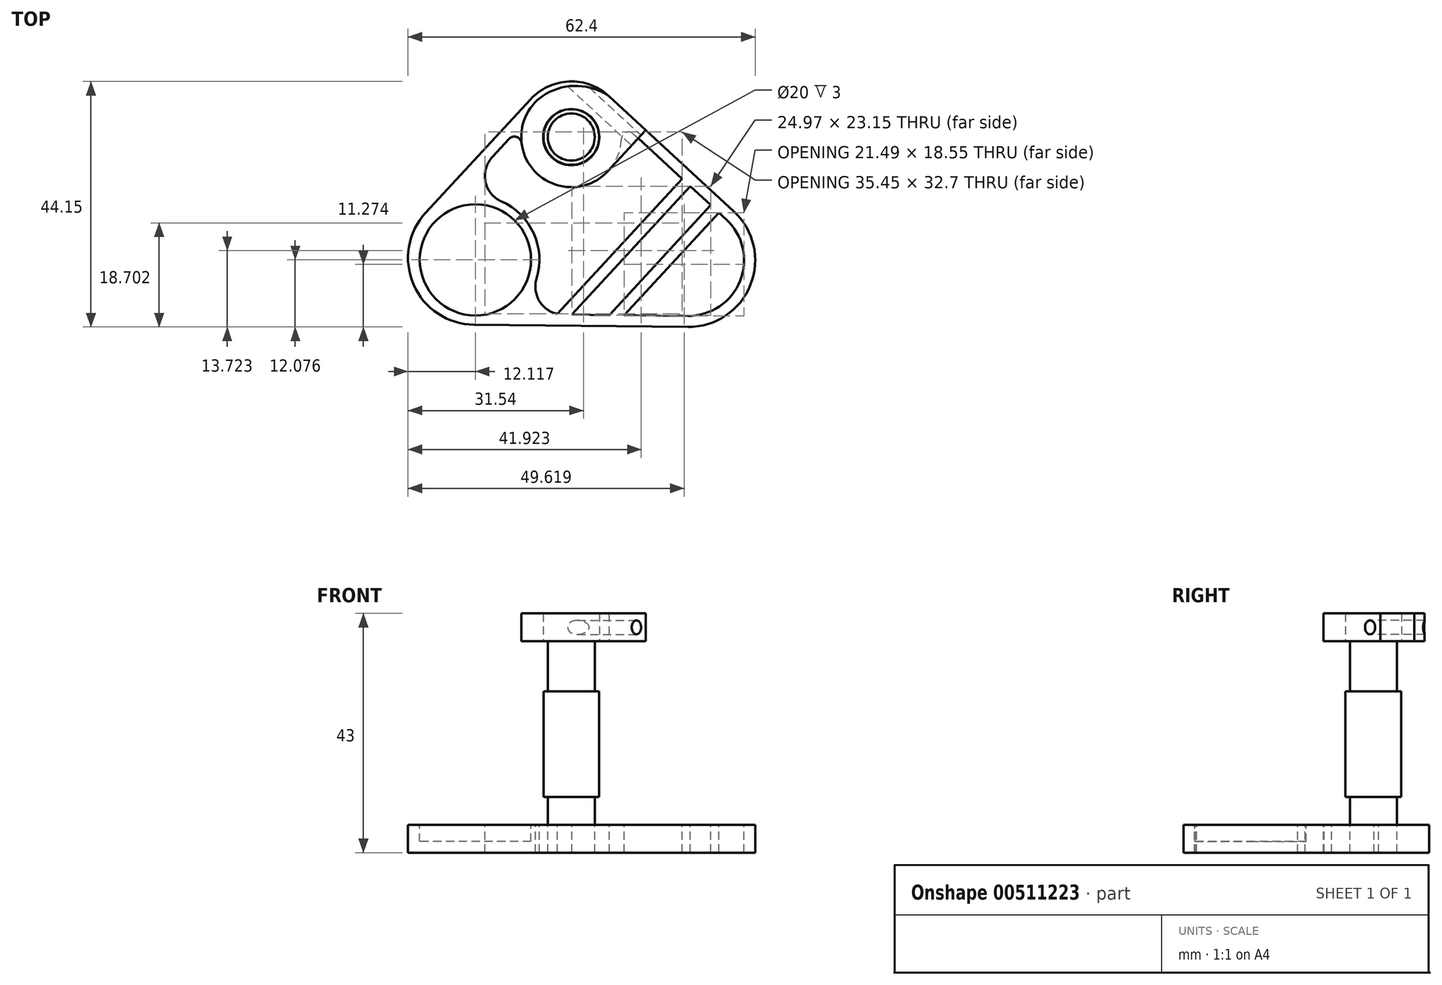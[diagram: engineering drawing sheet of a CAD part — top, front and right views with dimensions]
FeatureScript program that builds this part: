
annotation { "Feature Type Name" : "Feature", "Feature Type Description" : "" }
export const myFeature = defineFeature(function(context is Context, id is Id, definition is map)
    precondition{}
    {
        {
            var Q0;
            Q0=qCreatedBy(makeId("Top.planeOp"),FACE);
            var sketch = newSketch(context, id + "F0", { "sketchPlane" : qUnion([Q0])});
            skCircle(sketch, "E0", {"center": v(31.1, -55.05) * mm, "radius": 5 * mm});
            skCircle(sketch, "E1", {"center": v(31.1, -55.05) * mm, "radius": 4.22 * mm});
            skCircle(sketch, "E2", {"center": v(13.88, -77.12) * mm, "radius": 10 * mm});
            skPoint(sketch, "E3", {"position": v(54.93, -69.76) * mm});
            skLineSegment(sketch, "E4", {"start": v(23.76, -48.27) * mm, "end": v(4.95, -68.66) * mm});
            skLineSegment(sketch, "E5", {"start": v(37.89, -47.7) * mm, "end": v(60.3, -68.38) * mm});
            skLineSegment(sketch, "E6", {"start": v(52.03, -89.2) * mm, "end": v(13.64, -88.8) * mm});
            skArc(sketch, "E7.filletArc", {"start": v(4.95, -68.66) * mm, "mid": v(2.75, -81.55) * mm, "end": v(13.64, -88.8) * mm});
            skPoint(sketch, "E8.visualSharp", {"position": v(30.54, -40.92) * mm});
            skArc(sketch, "E8.filletArc", {"start": v(37.89, -47.7) * mm, "mid": v(30.7, -45.06) * mm, "end": v(23.76, -48.27) * mm});
            skArc(sketch, "E9.filletArc", {"start": v(52.03, -89.2) * mm, "mid": v(63.3, -81.63) * mm, "end": v(60.3, -68.38) * mm});
            skArc(sketch, "E10", {"start": v(22.17, -56.11) * mm, "mid": v(31.47, -64.05) * mm, "end": v(40.1, -55.4) * mm});
            skArc(sketch, "E11", {"start": v(24.87, -80.5) * mm, "mid": v(24.34, -72.35) * mm, "end": v(18.54, -66.61) * mm});
            skLineSegment(sketch, "E12", {"start": v(16.9, -58.65) * mm, "end": v(19.92, -55.38) * mm});
            skArc(sketch, "E13", {"start": v(52.05, -87.2) * mm, "mid": v(61.45, -80.9) * mm, "end": v(58.94, -69.85) * mm});
            skLineSegment(sketch, "E14", {"start": v(42.29, -54.48) * mm, "end": v(58.96, -69.87) * mm});
            skLineSegment(sketch, "E15", {"start": v(29.6, -86.96) * mm, "end": v(52.05, -87.2) * mm});
            skPoint(sketch, "E16.endSnap0", {"position": v(14.35, -58.46) * mm});
            skLineSegment(sketch, "E17", {"start": v(31.2, -86.98) * mm, "end": v(52.5, -63.9) * mm});
            skPoint(sketch, "E18.orphan", {"position": v(57.46, -58.46) * mm});
            skLineSegment(sketch, "E19.trimOffspring", {"start": v(28.5, -86.95) * mm, "end": v(51.02, -62.55) * mm});
            skLineSegment(sketch, "E20", {"start": v(37.94, -87.05) * mm, "end": v(56.17, -67.3) * mm});
            skLineSegment(sketch, "E21", {"start": v(40.63, -87.08) * mm, "end": v(57.64, -68.65) * mm});
            skPoint(sketch, "E22.visualSharp", {"position": v(9.76, -66.39) * mm});
            skArc(sketch, "E22.filletArc", {"start": v(16.9, -58.65) * mm, "mid": v(15.68, -63.06) * mm, "end": v(18.54, -66.61) * mm});
            skPoint(sketch, "E23.visualSharp", {"position": v(20, -86.86) * mm});
            skArc(sketch, "E23.filletArc", {"start": v(24.87, -80.5) * mm, "mid": v(25.62, -84.91) * mm, "end": v(29.6, -86.96) * mm});
            skArc(sketch, "E24.filletArc", {"start": v(22.17, -56.11) * mm, "mid": v(21.28, -55.03) * mm, "end": v(19.92, -55.38) * mm});
            skPoint(sketch, "E25.visualSharp", {"position": v(39.56, -51.97) * mm});
            skArc(sketch, "E25.filletArc", {"start": v(42.29, -54.48) * mm, "mid": v(40.9, -54.24) * mm, "end": v(40.1, -55.4) * mm});
            skSolve(sketch);
        }
        {
            var Q0;
            Q0=makeQuery(id+"F0.imprint","IMPRINT",FACE,{"disambiguationData":[TD([[makeQuery(id+"F0.imprint","IMPRINT",EDGE,{"derivedFrom":sQuery(id+"F0.wireOp",EDGE,"ScRWYDua-mYab-p1bD-zXnp-wvtpqM8LOkLs.bottom")}),-1.0]])]});
            var Q1;
            Q1=makeQuery(id+"F0.imprint","IMPRINT",FACE,{"disambiguationData":[TD([[makeQuery(id+"F0.imprint","IMPRINT",EDGE,{"derivedFrom":sQuery(id+"F0.wireOp",EDGE,"E2")}),1.0]])]});
            var Q2;
            Q2=makeQuery(id+"F0.imprint","IMPRINT",FACE,{"disambiguationData":[TD([[makeQuery(id+"F0.imprint","IMPRINT",EDGE,{"derivedFrom":sQuery(id+"F0.wireOp",EDGE,"W70nhKsN-JiaP-Kaip-Gnzn-Tj85YjjBPHD4.bottom")}),1.0]])]});
            var Q3;
            Q3=makeQuery(id+"F0.imprint","IMPRINT",FACE,{"disambiguationData":[TD([[makeQuery(id+"F0.imprint","IMPRINT",EDGE,{"derivedFrom":sQuery(id+"F0.wireOp",EDGE,"ScRWYDua-mYab-p1bD-zXnp-wvtpqM8LOkLs.top")}),1.0]])]});
            var Q4;
            Q4=makeQuery(id+"F0.imprint","IMPRINT",FACE,{"disambiguationData":[TD([[makeQuery(id+"F0.imprint","IMPRINT",EDGE,{"derivedFrom":sQuery(id+"F0.wireOp",EDGE,"E0")}),-1.0]])]});
            var Q5;
            {var subQ0=sQuery(id+"F0.wireOp",EDGE,"E17");Q5=makeQuery(id+"F0.imprint","IMPRINT",FACE,{"disambiguationData":[TD([[makeQuery(id+"F0.imprint","IMPRINT",EDGE,{"derivedFrom":subQ0}),1.0]])]});}
            var Q6;
            {var subQ0=sQuery(id+"F0.wireOp",EDGE,"E20");Q6=makeQuery(id+"F0.imprint","IMPRINT",FACE,{"disambiguationData":[TD([[makeQuery(id+"F0.imprint","IMPRINT",EDGE,{"derivedFrom":subQ0}),-1.0]])]});}
            var Q7;
            {var subQ0=sQuery(id+"F0.wireOp",EDGE,"thUjPLeQ-msCZ-fr84-VyUT-lr2uj8MLr4R7");Q7=makeQuery(id+"F0.imprint","IMPRINT",FACE,{"disambiguationData":[TD([[makeQuery(id+"F0.imprint","IMPRINT",EDGE,{"derivedFrom":subQ0}),-1.0]])]});}
            var Q8;
            Q8=makeQuery(id+"F0.imprint","IMPRINT",FACE,{"disambiguationData":[TD([[makeQuery(id+"F0.imprint","IMPRINT",EDGE,{"derivedFrom":sQuery(id+"F0.wireOp",EDGE,"E0")}),1.0]])]});
            extrude(context, id + "F1", {"entities" : qUnion([Q0, Q1, Q2, Q3, Q4, Q5, Q6, Q7, Q8]), "oppositeDirection" : true, "depth" : 5 * mm, "offsetDistance" : 25 * mm});
        }
        {
            var Q0;
            Q0=makeQuery(id+"F0.imprint","IMPRINT",FACE,{"disambiguationData":[TD([[makeQuery(id+"F0.imprint","IMPRINT",EDGE,{"derivedFrom":sQuery(id+"F0.wireOp",EDGE,"E1")}),1.0]])]});
            extrude(context, id + "F2", {"entities" : qUnion([Q0]), "depth" : 33 * mm, "offsetDistance" : 25 * mm});
        }
        {
            var Q0;
            Q0=makeQuery(id+"F0.imprint","IMPRINT",FACE,{"disambiguationData":[TD([[makeQuery(id+"F0.imprint","IMPRINT",EDGE,{"derivedFrom":sQuery(id+"F0.wireOp",EDGE,"E0")}),1.0]])]});
            extrude(context, id + "F3", {"entities" : qUnion([Q0]), "operationType" : NewBodyOperationType.ADD, "depth" : 24 * mm, "offsetDistance" : 25 * mm});
        }
        {
            var Q0;
            Q0=makeQuery(id+"F0.imprint","IMPRINT",FACE,{"disambiguationData":[TD([[makeQuery(id+"F0.imprint","IMPRINT",EDGE,{"derivedFrom":sQuery(id+"F0.wireOp",EDGE,"E2")}),1.0]])]});
            extrude(context, id + "F4", {"entities" : qUnion([Q0]), "operationType" : NewBodyOperationType.REMOVE, "oppositeDirection" : true, "depth" : 3 * mm});
        }
        {
            var Q0;
            Q0=makeQuery(id+"F0.imprint","IMPRINT",FACE,{"disambiguationData":[TD([[makeQuery(id+"F0.imprint","IMPRINT",EDGE,{"derivedFrom":sQuery(id+"F0.wireOp",EDGE,"E0")}),1.0]])]});
            extrude(context, id + "F5", {"entities" : qUnion([Q0]), "operationType" : NewBodyOperationType.REMOVE, "depth" : 5 * mm, "offsetDistance" : 25 * mm});
        }
        {
            var Q0;
            Q0=makeQuery(id+"F2.opExtrude","CAP_FACE",FACE,{"disambiguationData":[OSD([sQuery(id+"F0.wireOp",EDGE,"E1")])],"isStart":false});
            var sketch = newSketch(context, id + "F6", { "sketchPlane" : qUnion([Q0])});
            skCircle(sketch, "E26.0", {"center": v(31.1, -55.05) * mm, "radius": 5 * mm});
            skArc(sketch, "E26.1", {"start": v(22.17, -56.11) * mm, "mid": v(28.33, -63.61) * mm, "end": v(37.72, -61.16) * mm});
            skLineSegment(sketch, "E26.2", {"start": v(37.89, -47.7) * mm, "end": v(44.5, -53.8) * mm});
            skArc(sketch, "E27", {"start": v(26.6, -47.27) * mm, "mid": v(24.08, -60.68) * mm, "end": v(37.72, -61.16) * mm});
            skCircle(sketch, "E28", {"center": v(31.1, -55.05) * mm, "radius": 5.05 * mm});
            skArc(sketch, "E29", {"start": v(37.89, -47.7) * mm, "mid": v(32.3, -45.85) * mm, "end": v(26.6, -47.27) * mm});
            skLineSegment(sketch, "E30", {"start": v(37.72, -61.16) * mm, "end": v(43.15, -55.28) * mm});
            skLineSegment(sketch, "E31", {"start": v(43.15, -55.28) * mm, "end": v(44.5, -53.8) * mm});
            skSolve(sketch);
        }
        {
            var Q0;
            Q0 = qSketchRegion(id + "F6", true);
            extrude(context, id + "F7", {"entities" : qUnion([Q0]), "depth" : 5 * mm, "offsetDistance" : 25 * mm});
        }
        {
            var Q0;
            Q0=makeQuery(id+"F7.opExtrude","SWEPT_FACE",FACE,{"disambiguationData":[OSD([sQuery(id+"F6.wireOp",EDGE,"E30"),sQuery(id+"F6.wireOp",EDGE,"E31")])]});
            var sketch = newSketch(context, id + "F8", { "sketchPlane" : qUnion([Q0])});
            skCircle(sketch, "E32", {"center": v(-11.86, 35.5) * mm, "radius": 1.25 * mm});
            skSolve(sketch);
        }
        {
            var Q0;
            Q0 = qSketchRegion(id + "F8", true);
            extrude(context, id + "F9", {"entities" : qUnion([Q0]), "operationType" : NewBodyOperationType.REMOVE, "endBound" : BoundingType.THROUGH_ALL, "oppositeDirection" : true, "depth" : 25 * mm, "offsetDistance" : 25 * mm});
        }
    });
